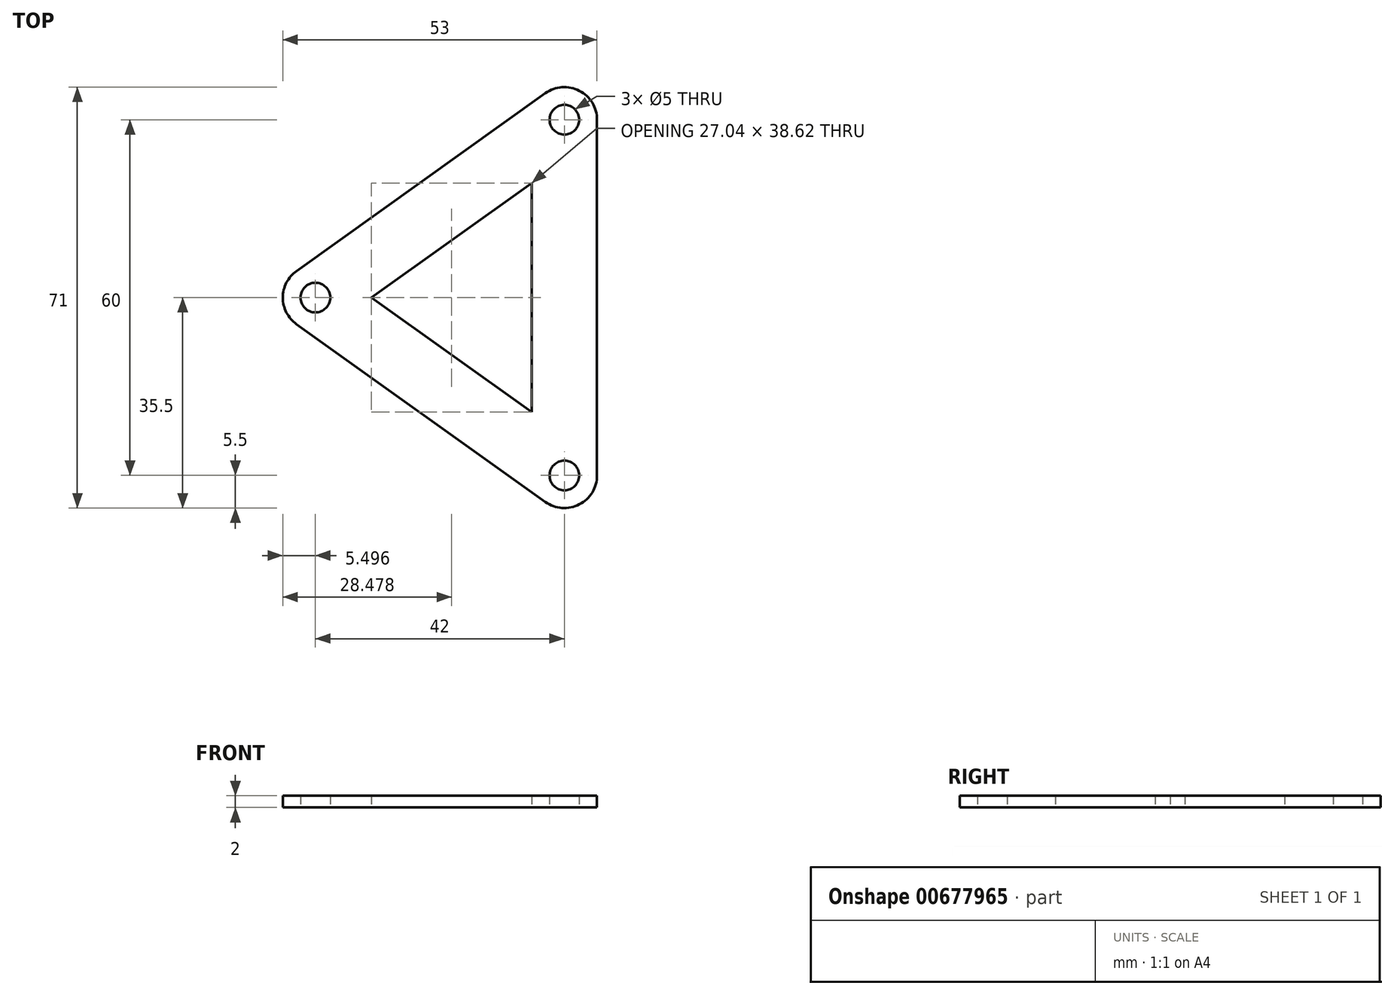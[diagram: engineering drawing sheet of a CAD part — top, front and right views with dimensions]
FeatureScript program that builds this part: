
annotation { "Feature Type Name" : "Feature", "Feature Type Description" : "" }
export const myFeature = defineFeature(function(context is Context, id is Id, definition is map)
    precondition{}
    {
        {
            var Q0;
            Q0=qCreatedBy(makeId("Top.planeOp"),FACE);
            var sketch = newSketch(context, id + "F0", { "sketchPlane" : qUnion([Q0])});
            skCircle(sketch, "E0", {"center": v(-17.31, 0) * mm, "radius": 2.5 * mm});
            skCircle(sketch, "E1", {"center": v(-17.31, 0) * mm, "radius": 5.5 * mm});
            skCircle(sketch, "E2", {"center": v(24.69, 30) * mm, "radius": 2.5 * mm});
            skCircle(sketch, "E3", {"center": v(24.69, 30) * mm, "radius": 5.5 * mm});
            skCircle(sketch, "E4", {"center": v(24.69, -30) * mm, "radius": 2.5 * mm});
            skCircle(sketch, "E5", {"center": v(24.69, -30) * mm, "radius": 5.5 * mm});
            skLineSegment(sketch, "E6", {"start": v(-17.31, 0) * mm, "end": v(24.69, 30) * mm, "construction": true});
            skLineSegment(sketch, "E7", {"start": v(-17.31, 0) * mm, "end": v(24.69, -30) * mm, "construction": true});
            skLineSegment(sketch, "E8", {"start": v(24.69, 30) * mm, "end": v(24.69, -30) * mm, "construction": true});
            skCircle(sketch, "E9", {"center": v(-17.31, 0) * mm, "radius": 4 * mm});
            skCircle(sketch, "E10", {"center": v(24.69, 30) * mm, "radius": 4 * mm});
            skCircle(sketch, "E11", {"center": v(24.69, -30) * mm, "radius": 4 * mm});
            skLineSegment(sketch, "E12.0", {"start": v(-7.85, 0) * mm, "end": v(19.19, 19.31) * mm});
            skLineSegment(sketch, "E12.1", {"start": v(-7.85, 0) * mm, "end": v(19.19, -19.31) * mm});
            skLineSegment(sketch, "E12.2", {"start": v(19.19, 19.31) * mm, "end": v(19.19, -19.31) * mm});
            skLineSegment(sketch, "E13.0", {"start": v(-20.51, 4.48) * mm, "end": v(21.49, 34.48) * mm});
            skLineSegment(sketch, "E13.1", {"start": v(-20.51, -4.48) * mm, "end": v(21.49, -34.48) * mm});
            skLineSegment(sketch, "E13.2", {"start": v(30.19, 30) * mm, "end": v(30.19, -30) * mm});
            skSolve(sketch);
        }
        {
            var Q0;
            Q0=makeQuery(id+"F0.imprint","IMPRINT",FACE,{"disambiguationData":[TD([[makeQuery(id+"F0.imprint","IMPRINT",EDGE,{"derivedFrom":sQuery(id+"F0.wireOp",EDGE,"E2")}),-1.0]])]});
            var Q1;
            {var subQ0=sQuery(id+"F0.wireOp",EDGE,"4292a800-b917-446e-8acb-4b11a4841fbd.0");var subQ1=sQuery(id+"F0.wireOp",EDGE,"E3");var subQ2=makeQuery(id+"F0.imprint","INTERSECT",VERTEX,{"derivedFrom":[subQ1,subQ0]});Q1=makeQuery(id+"F0.imprint","IMPRINT",FACE,{"disambiguationData":[TD([[makeQuery(id+"F0.imprint","IMPRINT",EDGE,{"disambiguationData":[TD([[subQ2,1.0]])],"derivedFrom":subQ1}),-1.0]])]});}
            var Q2;
            {var subQ0=sQuery(id+"F0.wireOp",EDGE,"b792d51c-0fe7-4bc2-b237-ce6525926208.0");Q2=makeQuery(id+"F0.imprint","IMPRINT",FACE,{"disambiguationData":[TD([[makeQuery(id+"F0.imprint","IMPRINT",EDGE,{"derivedFrom":subQ0}),-1.0]])]});}
            var Q3;
            Q3=makeQuery(id+"F0.imprint","IMPRINT",FACE,{"disambiguationData":[TD([[makeQuery(id+"F0.imprint","IMPRINT",EDGE,{"derivedFrom":sQuery(id+"F0.wireOp",EDGE,"E0")}),-1.0]])]});
            var Q4;
            {var subQ5=sQuery(id+"F0.wireOp",EDGE,"534e31a0-9855-4669-a3b1-e7b8400ff121.0");Q4=makeQuery(id+"F0.imprint","IMPRINT",FACE,{"disambiguationData":[TD([[makeQuery(id+"F0.imprint","IMPRINT",EDGE,{"derivedFrom":subQ5}),1.0]])]});}
            var Q5;
            {var subQ0=sQuery(id+"F0.wireOp",EDGE,"4292a800-b917-446e-8acb-4b11a4841fbd.0");var subQ1=sQuery(id+"F0.wireOp",EDGE,"E1");var subQ2=makeQuery(id+"F0.imprint","INTERSECT",VERTEX,{"derivedFrom":[subQ1,subQ0]});Q5=makeQuery(id+"F0.imprint","IMPRINT",FACE,{"disambiguationData":[TD([[makeQuery(id+"F0.imprint","IMPRINT",EDGE,{"disambiguationData":[TD([[subQ2,-1.0]])],"derivedFrom":subQ1}),-1.0]])]});}
            var Q6;
            {var subQ0=sQuery(id+"F0.wireOp",EDGE,"38d55559-1d0e-4463-9ff6-01328a6df294.0");var subQ1=sQuery(id+"F0.wireOp",EDGE,"E5");var subQ2=makeQuery(id+"F0.imprint","INTERSECT",VERTEX,{"derivedFrom":[subQ1,subQ0]});Q6=makeQuery(id+"F0.imprint","IMPRINT",FACE,{"disambiguationData":[TD([[makeQuery(id+"F0.imprint","IMPRINT",EDGE,{"disambiguationData":[TD([[subQ2,-1.0]])],"derivedFrom":subQ1}),-1.0]])]});}
            var Q7;
            Q7=makeQuery(id+"F0.imprint","IMPRINT",FACE,{"disambiguationData":[TD([[makeQuery(id+"F0.imprint","IMPRINT",EDGE,{"derivedFrom":sQuery(id+"F0.wireOp",EDGE,"E4")}),-1.0]])]});
            var Q8;
            {var subQ9=sQuery(id+"F0.wireOp",EDGE,"a9f5d0ef-61d3-43a7-a030-e22b1175c3c5.0");Q8=makeQuery(id+"F0.imprint","IMPRINT",FACE,{"disambiguationData":[TD([[makeQuery(id+"F0.imprint","IMPRINT",EDGE,{"derivedFrom":subQ9}),-1.0]])]});}
            var Q9;
            Q9=makeQuery(id+"F0.imprint","IMPRINT",FACE,{"disambiguationData":[TD([[makeQuery(id+"F0.imprint","IMPRINT",EDGE,{"derivedFrom":sQuery(id+"F0.wireOp",EDGE,"E11")}),-1.0]])]});
            var Q10;
            Q10=makeQuery(id+"F0.imprint","IMPRINT",FACE,{"disambiguationData":[TD([[makeQuery(id+"F0.imprint","IMPRINT",EDGE,{"derivedFrom":sQuery(id+"F0.wireOp",EDGE,"E9")}),-1.0]])]});
            var Q11;
            Q11=makeQuery(id+"F0.imprint","IMPRINT",FACE,{"disambiguationData":[TD([[makeQuery(id+"F0.imprint","IMPRINT",EDGE,{"derivedFrom":sQuery(id+"F0.wireOp",EDGE,"E10")}),-1.0]])]});
            extrude(context, id + "F1", {"entities" : qUnion([Q0, Q1, Q2, Q3, Q4, Q5, Q6, Q7, Q8, Q9, Q10, Q11]), "depth" : 2 * mm, "offsetDistance" : 25 * mm});
        }
    });
